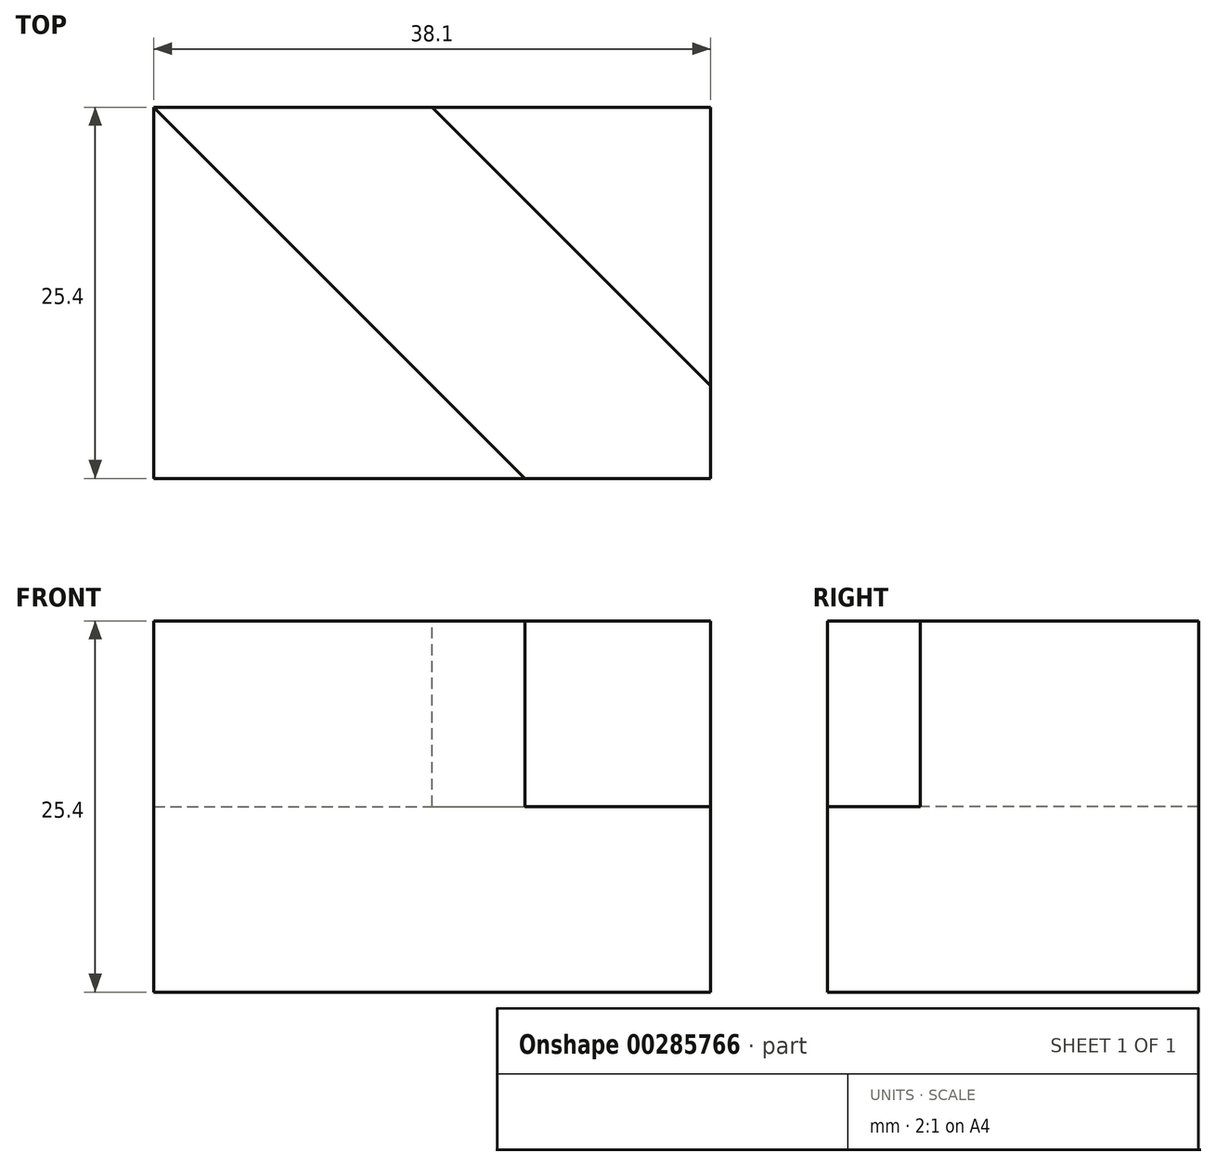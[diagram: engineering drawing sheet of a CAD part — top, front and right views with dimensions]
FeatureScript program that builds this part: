
annotation { "Feature Type Name" : "Feature", "Feature Type Description" : "" }
export const myFeature = defineFeature(function(context is Context, id is Id, definition is map)
    precondition{}
    {
        {
            var Q0;
            Q0=qCreatedBy(makeId("Front.planeOp"),FACE);
            var sketch = newSketch(context, id + "F0", { "sketchPlane" : qUnion([Q0])});
            skLineSegment(sketch, "E0.bottom", {"start": v(0, 0) * mm, "end": v(38.1, 0) * mm});
            skLineSegment(sketch, "E0.top", {"start": v(0, 25.4) * mm, "end": v(38.1, 25.4) * mm});
            skLineSegment(sketch, "E0.left", {"start": v(0, 0) * mm, "end": v(0, 25.4) * mm});
            skLineSegment(sketch, "E0.right", {"start": v(38.1, 0) * mm, "end": v(38.1, 25.4) * mm});
            skSolve(sketch);
        }
        {
            var Q0;
            Q0 = qSketchRegion(id + "F0", true);
            extrude(context, id + "F1", {"entities" : qUnion([Q0]), "endBound" : BoundingType.SYMMETRIC, "depth" : 25.4 * mm});
        }
        {
            var Q0;
            Q0=makeQuery(id+"F1.opExtrude","SWEPT_FACE",FACE,{"disambiguationData":[OSD([sQuery(id+"F0.wireOp",EDGE,"E0.top")])]});
            var sketch = newSketch(context, id + "F2", { "sketchPlane" : qUnion([Q0])});
            skLineSegment(sketch, "E1", {"start": v(0, 12.7) * mm, "end": v(25.4, -12.7) * mm});
            skLineSegment(sketch, "E2", {"start": v(19.05, 12.7) * mm, "end": v(38.1, -6.35) * mm});
            skSolve(sketch);
        }
        {
            var Q0;
            {var subQ5=sQuery(id+"F2.wireOp",EDGE,"E1");Q0=makeQuery(id+"F2.imprint","IMPRINT",FACE,{"disambiguationData":[TD([[makeQuery(id+"F2.imprint","IMPRINT",EDGE,{"derivedFrom":subQ5}),1.0]])]});}
            extrude(context, id + "F3", {"entities" : qUnion([Q0]), "operationType" : NewBodyOperationType.REMOVE, "oppositeDirection" : true, "depth" : 12.7 * mm});
        }
    });
